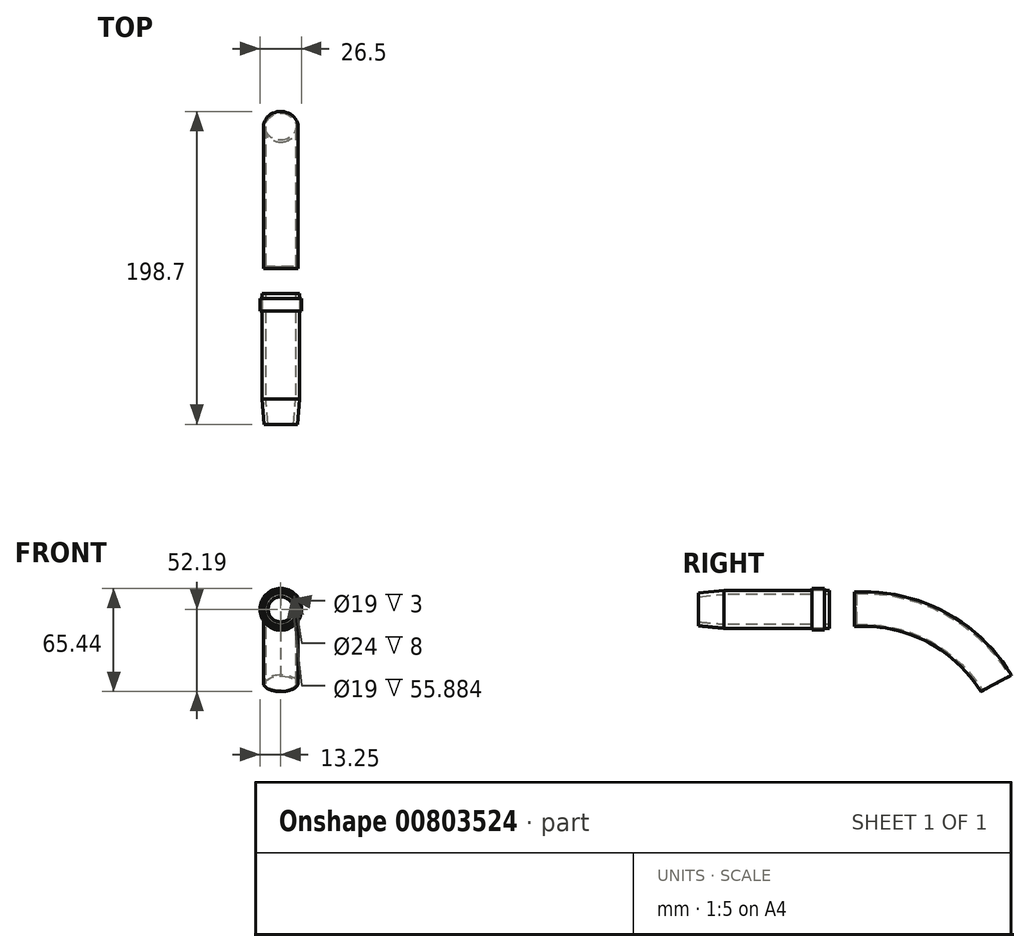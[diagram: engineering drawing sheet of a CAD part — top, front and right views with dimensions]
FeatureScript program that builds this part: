
annotation { "Feature Type Name" : "Feature", "Feature Type Description" : "" }
export const myFeature = defineFeature(function(context is Context, id is Id, definition is map)
    precondition{}
    {
        {
            var Q0;
            Q0=qCreatedBy(makeId("Front.planeOp"),FACE);
            var sketch = newSketch(context, id + "F0", { "sketchPlane" : qUnion([Q0])});
            skCircle(sketch, "E0", {"center": v(0, 0) * mm, "radius": 12 * mm});
            skSolve(sketch);
        }
        {
            var Q0;
            Q0=makeQuery(id+"F0.imprint","IMPRINT",FACE,{"disambiguationData":[TD([[makeQuery(id+"F0.imprint","IMPRINT",EDGE,{"derivedFrom":sQuery(id+"F0.wireOp",EDGE,"E0")}),1.0]])]});
            extrude(context, id + "F1", {"entities" : qUnion([Q0]), "oppositeDirection" : true, "depth" : 56 * mm, "offsetDistance" : 25 * mm});
        }
        {
            var Q0;
            Q0=makeQuery(id+"F1.opExtrude","CAP_FACE",FACE,{"disambiguationData":[OSD([sQuery(id+"F0.wireOp",EDGE,"E0")])],"isStart":true});
            var sketch = newSketch(context, id + "F2", { "sketchPlane" : qUnion([Q0])});
            skCircle(sketch, "E1.0.0", {"center": v(0, 0) * mm, "radius": 12 * mm});
            skSolve(sketch);
        }
        {
            var Q0;
            Q0 = qSketchRegion(id + "F2", true);
            extrude(context, id + "F3", {"entities" : qUnion([Q0]), "operationType" : NewBodyOperationType.ADD, "depth" : 16 * mm, "offsetDistance" : 25 * mm, "hasDraft" : true, "draftAngle" : 5.3 * degree, "draftPullDirection" : true});
        }
        {
            var Q0;
            Q0=makeQuery(id+"F3.opExtrude","CAP_FACE",FACE,{"disambiguationData":[OSD([sQuery(id+"F2.wireOp",EDGE,"E1.0.0")])],"isStart":false});
            var Q1;
            Q1=makeQuery(id+"F1.opExtrude","CAP_FACE",FACE,{"disambiguationData":[OSD([sQuery(id+"F0.wireOp",EDGE,"E0")])],"isStart":false});
            shell(context, id + "F4", {"entities" : qUnion([Q0, Q1]), "thickness" : 2.5 * mm});
        }
        {
            var Q0;
            Q0=makeQuery(id+"F1.opExtrude","CAP_FACE",FACE,{"disambiguationData":[OSD([sQuery(id+"F0.wireOp",EDGE,"E0")])],"isStart":false});
            var sketch = newSketch(context, id + "F5", { "sketchPlane" : qUnion([Q0])});
            skCircle(sketch, "E2.0", {"center": v(0, 0) * mm, "radius": 12 * mm});
            skCircle(sketch, "E3", {"center": v(0, 0) * mm, "radius": 13.25 * mm});
            skSolve(sketch);
        }
        {
            var Q0;
            Q0 = qSketchRegion(id + "F5", true);
            extrude(context, id + "F6", {"entities" : qUnion([Q0]), "depth" : 8 * mm, "offsetDistance" : 25 * mm});
        }
        {
            var Q0;
            Q0=makeQuery(id+"F6.opExtrude","CAP_FACE",FACE,{"disambiguationData":[OSD([sQuery(id+"F5.wireOp",EDGE,"E2.0"),sQuery(id+"F5.wireOp",EDGE,"E3")])],"isStart":false});
            var sketch = newSketch(context, id + "F7", { "sketchPlane" : qUnion([Q0])});
            skCircle(sketch, "E4.0", {"center": v(0, 0) * mm, "radius": 12 * mm});
            skCircle(sketch, "E5.0", {"center": v(0, 0) * mm, "radius": 9.5 * mm});
            skSolve(sketch);
        }
        {
            var Q0;
            Q0 = qSketchRegion(id + "F7", true);
            extrude(context, id + "F8", {"entities" : qUnion([Q0]), "depth" : 3 * mm, "offsetDistance" : 25 * mm});
        }
        {
            var Q0;
            Q0=qCreatedBy(makeId("Top.planeOp"),FACE);
            var sketch = newSketch(context, id + "F9", { "sketchPlane" : qUnion([Q0])});
            skLineSegment(sketch, "E6.0", {"start": v(0, 67) * mm, "end": v(-12, 67) * mm});
            skLineSegment(sketch, "E7", {"start": v(-12, 67) * mm, "end": v(-12.5, 67) * mm});
            skLineSegment(sketch, "E8", {"start": v(-12.5, 67) * mm, "end": v(-12.5, 68.45) * mm});
            skLineSegment(sketch, "E9", {"start": v(-12.5, 68.45) * mm, "end": v(-9.7, 68.45) * mm});
            skLineSegment(sketch, "E10", {"start": v(-9.7, 68.45) * mm, "end": v(-9.7, 70.95) * mm});
            skLineSegment(sketch, "E11", {"start": v(-9.7, 70.95) * mm, "end": v(-12.5, 70.95) * mm});
            skPoint(sketch, "E12.orphan", {"position": v(12, 67) * mm});
            skPoint(sketch, "E13.orphan", {"position": v(0, 83.05) * mm});
            skLineSegment(sketch, "E14.trimOffspring", {"start": v(0, 83) * mm, "end": v(0, 67) * mm});
            skLineSegment(sketch, "E15", {"start": v(-12.5, 70.95) * mm, "end": v(-12.5, 72.4) * mm});
            skLineSegment(sketch, "E16", {"start": v(-12.5, 72.4) * mm, "end": v(-9.7, 72.4) * mm});
            skLineSegment(sketch, "E17", {"start": v(-9.7, 72.4) * mm, "end": v(-9.7, 74.4) * mm});
            skLineSegment(sketch, "E18", {"start": v(-9.7, 74.4) * mm, "end": v(-12.5, 74.4) * mm});
            skLineSegment(sketch, "E19", {"start": v(-12.5, 74.4) * mm, "end": v(-12.5, 75.85) * mm});
            skLineSegment(sketch, "E20", {"start": v(-12.5, 75.85) * mm, "end": v(-9.7, 75.85) * mm});
            skLineSegment(sketch, "E21", {"start": v(-9.7, 75.85) * mm, "end": v(-9.7, 77.85) * mm});
            skLineSegment(sketch, "E22", {"start": v(-9.7, 77.85) * mm, "end": v(-12.5, 77.85) * mm});
            skLineSegment(sketch, "E23", {"start": v(-12.5, 77.85) * mm, "end": v(-12.5, 79.3) * mm});
            skLineSegment(sketch, "E24", {"start": v(-12.5, 79.3) * mm, "end": v(-9.7, 79.3) * mm});
            skLineSegment(sketch, "E25", {"start": v(-9.7, 79.3) * mm, "end": v(-9.7, 81.3) * mm});
            skLineSegment(sketch, "E26", {"start": v(-9.7, 81.3) * mm, "end": v(-11, 81.3) * mm});
            skLineSegment(sketch, "E27", {"start": v(-11, 81.3) * mm, "end": v(-11, 83) * mm});
            skLineSegment(sketch, "E28", {"start": v(-11, 83) * mm, "end": v(0, 83) * mm});
            skPoint(sketch, "E29.start.orphan", {"position": v(0, 100.83) * mm});
            skSolve(sketch);
        }
        {
            var Q0;
            Q0=sQuery(id+"F9.wireOp",EDGE,"E24");
            var Q1;
            Q1=sQuery(id+"F9.wireOp",EDGE,"E23");
            var Q2;
            Q2=sQuery(id+"F9.wireOp",EDGE,"E22");
            var Q3;
            Q3=sQuery(id+"F9.wireOp",EDGE,"E25");
            var Q4;
            Q4=sQuery(id+"F9.wireOp",EDGE,"E26");
            var Q5;
            Q5=sQuery(id+"F9.wireOp",EDGE,"E27");
            var Q6;
            Q6=sQuery(id+"F9.wireOp",EDGE,"E28");
            var Q7;
            Q7=sQuery(id+"F9.wireOp",EDGE,"E21");
            var Q8;
            Q8=sQuery(id+"F9.wireOp",EDGE,"E20");
            var Q9;
            Q9=sQuery(id+"F9.wireOp",EDGE,"E19");
            var Q10;
            Q10=sQuery(id+"F9.wireOp",EDGE,"E18");
            var Q11;
            Q11=sQuery(id+"F9.wireOp",EDGE,"E17");
            var Q12;
            Q12=sQuery(id+"F9.wireOp",EDGE,"E16");
            var Q13;
            Q13=sQuery(id+"F9.wireOp",EDGE,"E15");
            var Q14;
            Q14=sQuery(id+"F9.wireOp",EDGE,"E11");
            var Q15;
            Q15=sQuery(id+"F9.wireOp",EDGE,"E10");
            var Q16;
            Q16=sQuery(id+"F9.wireOp",EDGE,"E9");
            var Q17;
            Q17=sQuery(id+"F9.wireOp",EDGE,"E8");
            var Q18;
            Q18=sQuery(id+"F9.wireOp",EDGE,"E7");
            var Q19;
            Q19=sQuery(id+"F9.wireOp",EDGE,"E6.0");
            var Q20;
            Q20=sQuery(id+"F9.wireOp",EDGE,"E14.trimOffspring");
            revolve(context, id + "F10", {"bodyType" : ToolBodyType.SURFACE, "surfaceOperationType" : NewSurfaceOperationType.NEW, "surfaceEntities" : qUnion([Q0, Q1, Q2, Q3, Q4, Q5, Q6, Q7, Q8, Q9, Q10, Q11, Q12, Q13, Q14, Q15, Q16, Q17, Q18, Q19]), "axis" : qUnion([Q20]), "revolveType" : RevolveType.FULL});
        }
        {
            var Q0;
            Q0=qCreatedBy(makeId("Right.planeOp"),FACE);
            var sketch = newSketch(context, id + "F11", { "sketchPlane" : qUnion([Q0])});
            skArc(sketch, "E30", {"start": v(173, -47) * mm, "mid": v(134.5, -11.05) * mm, "end": v(83, 0) * mm});
            skPoint(sketch, "E30.third.point", {"position": v(94.55, 0) * mm});
            skPoint(sketch, "E31.orphan", {"position": v(83, 0) * mm});
            skPoint(sketch, "E32.orphan", {"position": v(83, 11) * mm});
            skPoint(sketch, "E33.0.start.orphan", {"position": v(83, -11) * mm});
            skSolve(sketch);
        }
        {
            var Q0;
            Q0=makeQuery(id+"F10.opRevolve","SWEPT_FACE",FACE,{"disambiguationData":[OSD([sQuery(id+"F9.wireOp",EDGE,"E28")])]});
            var sketch = newSketch(context, id + "F12", { "sketchPlane" : qUnion([Q0])});
            skCircle(sketch, "E34.0.0", {"center": v(0, 0) * mm, "radius": 11 * mm});
            skSolve(sketch);
        }
        {
            var Q0;
            Q0=makeQuery(id+"F12.imprint","IMPRINT",FACE,{"disambiguationData":[TD([[makeQuery(id+"F12.imprint","IMPRINT",EDGE,{"derivedFrom":sQuery(id+"F12.wireOp",EDGE,"E34.0.0")}),-1.0]])]});
            var Q1;
            Q1=sQuery(id+"F11.wireOp",EDGE,"E30");
            sweep(context, id + "F13", {"profiles" : qUnion([Q0]), "path" : qUnion([Q1])});
        }
        {
            var Q0;
            Q0=makeQuery(id+"F13.opSweep","CAP_FACE",FACE,{"disambiguationData":[OSD([sQuery(id+"F11.wireOp",VERTEX,"E30.start"),sQuery(id+"F12.wireOp",EDGE,"E34.0.0")])],"isStart":false});
            shell(context, id + "F14", {"entities" : qUnion([Q0]), "thickness" : 1.2 * mm});
        }
    });
